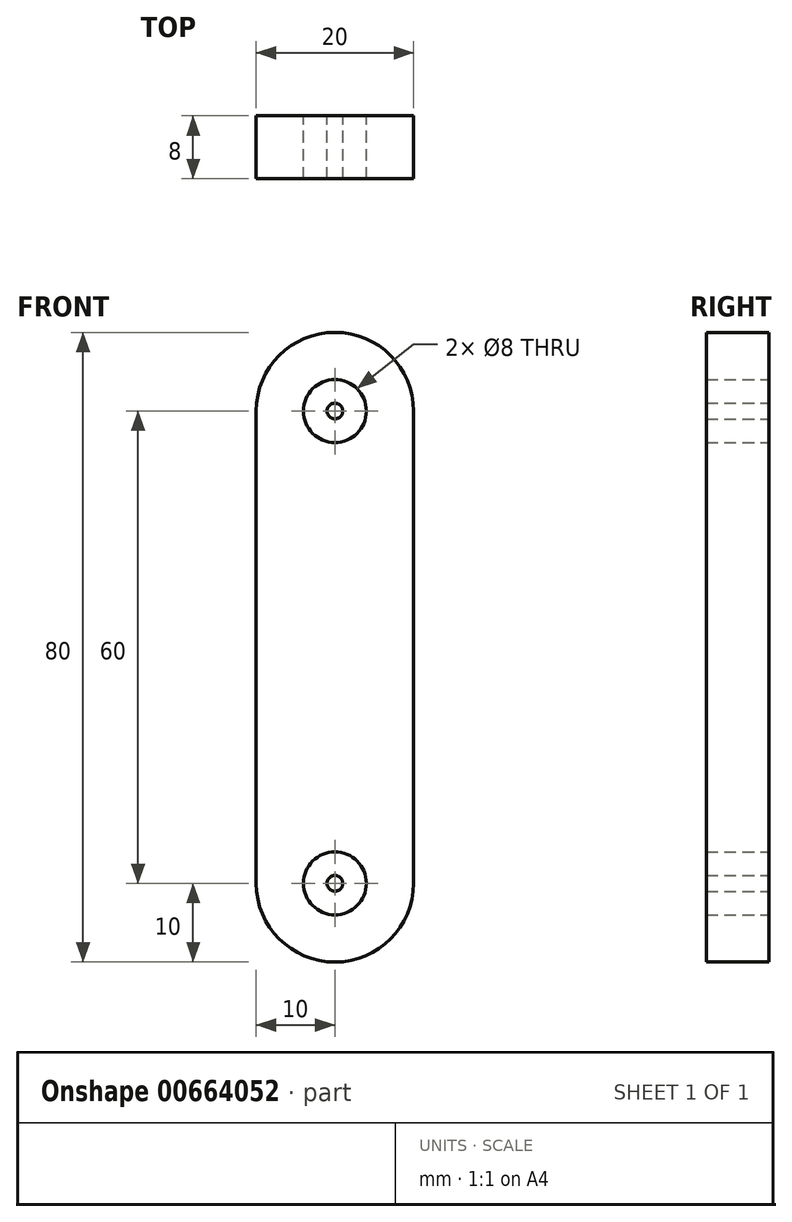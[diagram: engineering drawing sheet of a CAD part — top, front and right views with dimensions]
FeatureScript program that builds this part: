
annotation { "Feature Type Name" : "Feature", "Feature Type Description" : "" }
export const myFeature = defineFeature(function(context is Context, id is Id, definition is map)
    precondition{}
    {
        {
            var Q0;
            Q0=qCreatedBy(makeId("Front.planeOp"),FACE);
            var sketch = newSketch(context, id + "F0", { "sketchPlane" : qUnion([Q0])});
            skArc(sketch, "E0", {"start": v(-10, 0) * mm, "mid": v(0, -10) * mm, "end": v(10, 0) * mm});
            skLineSegment(sketch, "E1", {"start": v(-10, 0) * mm, "end": v(-10, 60) * mm});
            skLineSegment(sketch, "E2", {"start": v(10, 0) * mm, "end": v(10, 60) * mm});
            skArc(sketch, "E3", {"start": v(10, 60) * mm, "mid": v(0, 70) * mm, "end": v(-10, 60) * mm});
            skCircle(sketch, "E4", {"center": v(0, 60) * mm, "radius": 4 * mm});
            skCircle(sketch, "E5", {"center": v(0, 0) * mm, "radius": 4 * mm});
            skSolve(sketch);
        }
        {
            var Q0;
            Q0 = qSketchRegion(id + "F0", true);
            extrude(context, id + "F1", {"entities" : qUnion([Q0]), "depth" : 8 * mm, "offsetDistance" : 25.4 * mm});
        }
        {
            var Q0;
            Q0=qCreatedBy(makeId("Front.planeOp"),FACE);
            var sketch = newSketch(context, id + "F2", { "sketchPlane" : qUnion([Q0])});
            skCircle(sketch, "E6", {"center": v(0, 0) * mm, "radius": 1 * mm});
            skCircle(sketch, "E7", {"center": v(0, 60) * mm, "radius": 1 * mm});
            skSolve(sketch);
        }
        {
            var Q0;
            Q0 = qSketchRegion(id + "F2", true);
            extrude(context, id + "F3", {"entities" : qUnion([Q0]), "depth" : 8 * mm, "offsetDistance" : 25.4 * mm});
        }
    });
